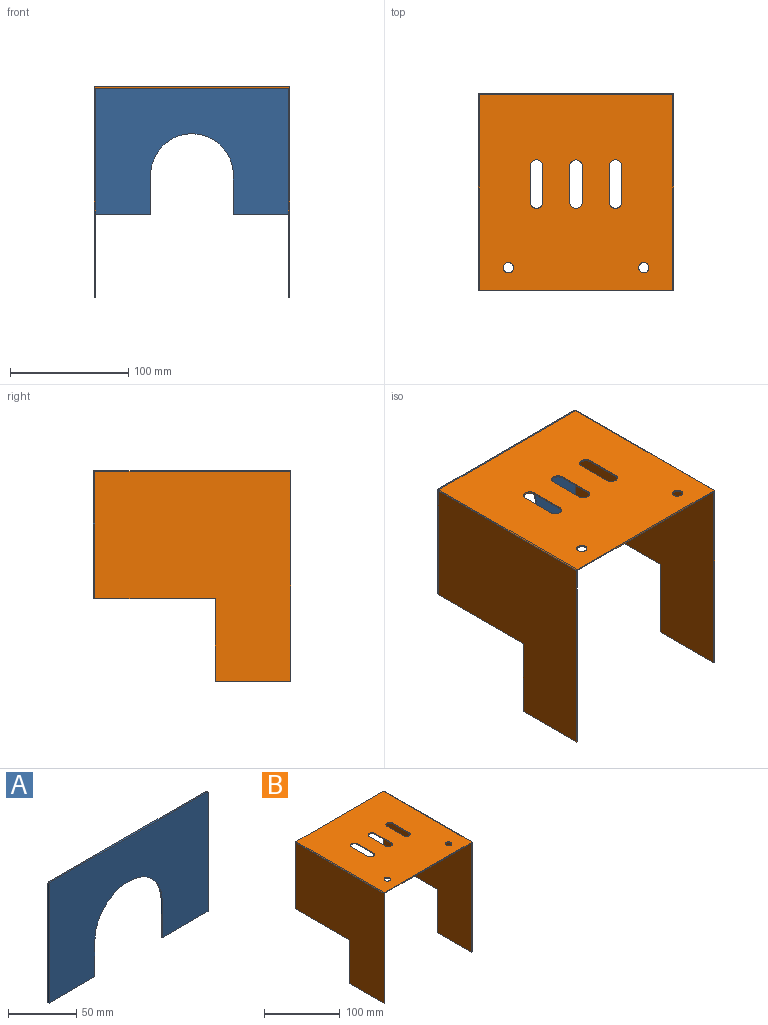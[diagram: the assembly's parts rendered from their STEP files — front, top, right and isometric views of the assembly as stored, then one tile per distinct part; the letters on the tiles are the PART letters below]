
ASSEMBLY  parts=2 mates=1
PART A: 12 faces, bbox 165.1x1.2x108 mm
  f0: plane 47.63x1.18mm, normal (0,0,-1), area 56.2mm2, adj f1,f5,f8,f9
  f1: plane 165.1x107.95mm, normal (0,1,0), area 13585mm2, adj f0,f2,f3,f4,f5,f6,f7,f9
  f2: cylinder r=0.79mm len=1.18mm, axis (0,-1,0), area 1.5mm2, adj f1,f3,f7,f8
  f3: plane 107.16x1.18mm, normal (1,0,0), area 126.6mm2, adj f1,f2,f4,f8
  f4: plane 47.63x1.18mm, normal (0,0,-1), area 56.2mm2, adj f1,f3,f8,f10
  f5: plane 107.16x1.18mm, normal (-1,0,0), area 126.6mm2, adj f0,f1,f6,f8
  f6: cylinder r=0.79mm len=1.18mm, axis (0,-1,0), area 1.5mm2, adj f1,f5,f7,f8
  f7: plane 163.51x1.18mm, normal (0,0,1), area 193.1mm2, adj f1,f2,f6,f8
  f8: plane 165.1x107.95mm, normal (0,-1,0), area 13585mm2, adj f0,f2,f3,f4,f5,f6,f7,f9
  f9: plane 33.24x1.18mm, normal (1,0,0), area 39.3mm2, adj f0,f1,f8,f11
  f10: plane 34.31x1.18mm, normal (-1,0,0), area 40.5mm2, adj f1,f4,f8,f11
  f11: cylinder r=34.92mm len=69.83mm, axis (0,1,0), area 128.3mm2, adj f1,f8,f9,f10
PART B: 32 faces, bbox 165.1x165.1x177.8 mm
  f0: plane 165.1x161.94mm, normal (0,0,-1), area 25392.7mm2, adj f6,f7,f12,f13,f18,f19,f20,f21
  f1: plane 165.1x163.51mm, normal (0,0,1), area 25651.6mm2, adj f10,f11,f12,f13,f18,f19,f20,f21
  f2: plane 63.5x1.18mm, normal (0,0,-1), area 75mm2, adj f8,f9,f13,f15
  f3: plane 177.01x165.1mm, normal (-1,0,0), area 22127mm2, adj f4,f11,f12,f13,f16,f17
  f4: plane 63.5x1.18mm, normal (0,0,-1), area 75mm2, adj f3,f5,f13,f16
  f5: plane 176.22x165.1mm, normal (1,0,0), area 21997.5mm2, adj f4,f6,f12,f13,f16,f17
  f6: cylinder r=0.4mm len=165.1mm, axis (0,-1,0), area 102.9mm2, adj f0,f5,f12,f13
  f7: cylinder r=0.4mm len=165.1mm, axis (0,-1,0), area 102.9mm2, adj f0,f8,f12,f13
  f8: plane 176.22x165.1mm, normal (-1,0,0), area 21997.5mm2, adj f2,f7,f12,f13,f14,f15
  f9: plane 177.01x165.1mm, normal (1,0,0), area 22127mm2, adj f2,f10,f12,f13,f14,f15
  f10: cylinder r=0.79mm len=165.1mm, axis (0,-1,0), area 205.8mm2, adj f1,f9,f12,f13
  f11: cylinder r=0.79mm len=165.1mm, axis (0,-1,0), area 205.8mm2, adj f1,f3,f12,f13
  f12: plane 165.1x107.95mm, normal (0,1,0), area 447mm2, adj f0,f1,f3,f5,f6,f7,f8,f9
  f13: plane 177.8x165.1mm, normal (0,-1,0), area 612mm2, adj f0,f1,f2,f3,f4,f5,f6,f7
  f14: plane 101.6x1.18mm, normal (0,0,-1), area 120mm2, adj f8,f9,f12,f15
  f15: plane 69.85x1.18mm, normal (0,1,0), area 82.5mm2, adj f2,f8,f9,f14
  f16: plane 69.85x1.18mm, normal (0,1,0), area 82.5mm2, adj f3,f4,f5,f17
  f17: plane 101.6x1.18mm, normal (0,0,-1), area 120mm2, adj f3,f5,f12,f16
  f18: cylinder r=5.3mm len=10.6mm, axis (0,0,1), area 19.7mm2, adj f0,f1,f19,f21
  f19: plane 30.16x1.18mm, normal (-1,0,0), area 35.6mm2, adj f0,f1,f18,f20
  f20: cylinder r=5.3mm len=10.6mm, axis (0,0,1), area 19.7mm2, adj f0,f1,f19,f21
  f21: plane 30.16x1.18mm, normal (1,0,0), area 35.6mm2, adj f0,f1,f18,f20
  f22: cylinder r=5.3mm len=10.6mm, axis (0,0,1), area 19.7mm2, adj f0,f1,f23,f25
  f23: plane 30.16x1.18mm, normal (-1,0,0), area 35.6mm2, adj f0,f1,f22,f24
  f24: cylinder r=5.3mm len=10.6mm, axis (0,0,1), area 19.7mm2, adj f0,f1,f23,f25
  f25: plane 30.16x1.18mm, normal (1,0,0), area 35.6mm2, adj f0,f1,f22,f24
  f26: cylinder r=5.3mm len=10.6mm, axis (0,0,1), area 19.7mm2, adj f0,f1,f27,f29
  f27: plane 30.16x1.18mm, normal (-1,0,0), area 35.6mm2, adj f0,f1,f26,f28
  f28: cylinder r=5.3mm len=10.6mm, axis (0,0,1), area 19.7mm2, adj f0,f1,f27,f29
  f29: plane 30.16x1.18mm, normal (1,0,0), area 35.6mm2, adj f0,f1,f26,f28
  f30: cylinder r=4.37mm len=8.73mm, axis (0,0,1), area 32.4mm2, adj f0,f1
  f31: cylinder r=4.37mm len=8.73mm, axis (0,0,1), area 32.4mm2, adj f0,f1
PLACE A t=(0,0,177.8)mm
PLACE B t=(0,0,177.8)mm
MATE fastened A.f8 <-> B.f12  axis (0,-1,0) through (165.1,165.1,69.85)mm
